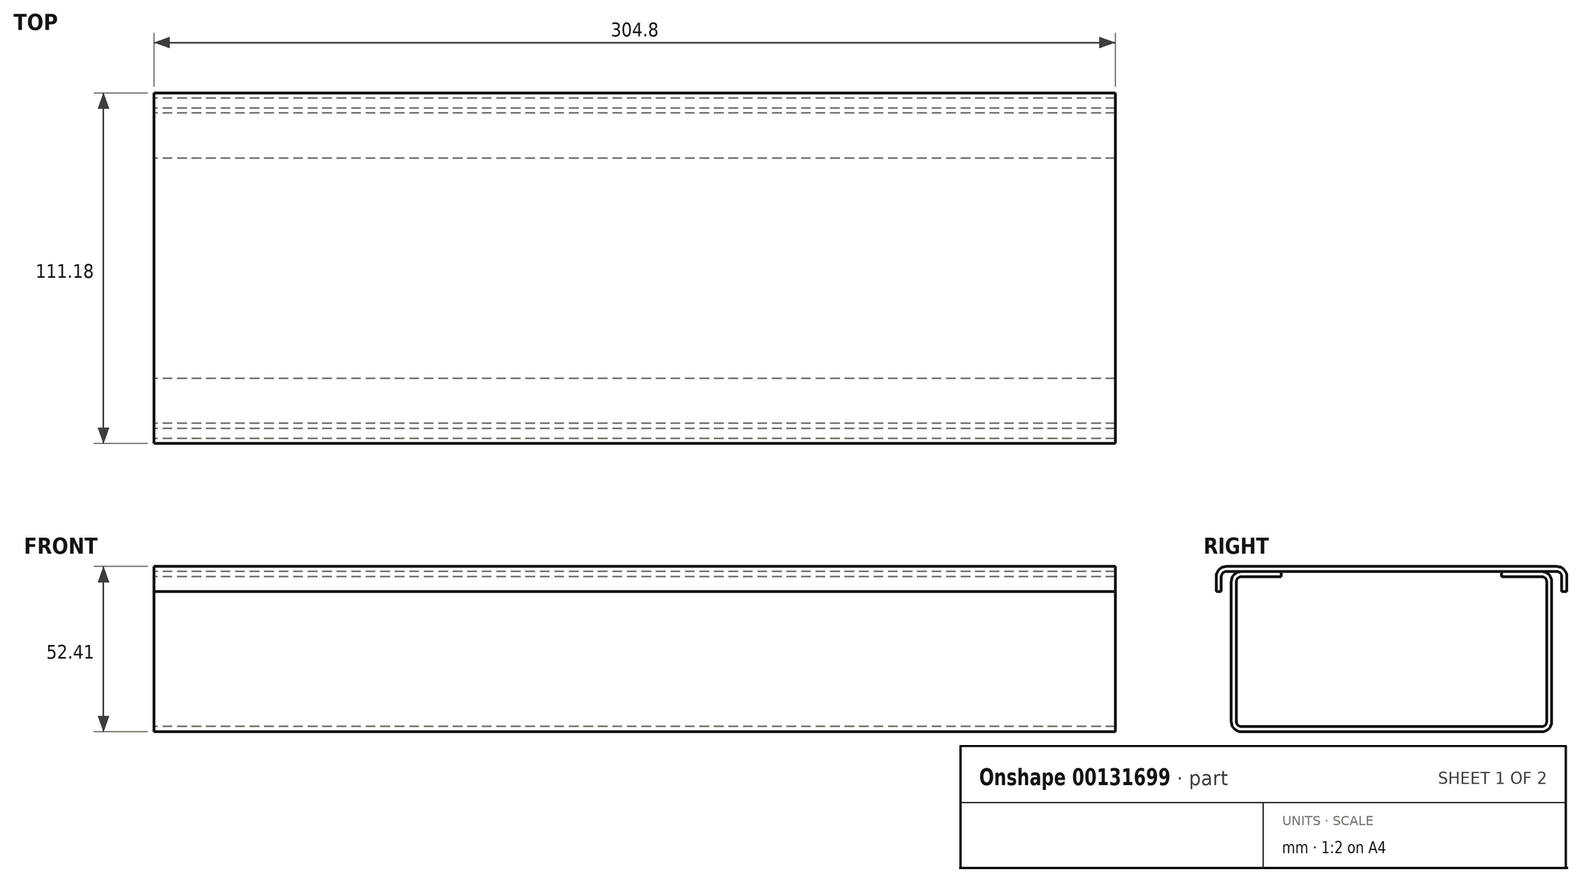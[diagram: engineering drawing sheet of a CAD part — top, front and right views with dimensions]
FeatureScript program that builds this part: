
annotation { "Feature Type Name" : "Feature", "Feature Type Description" : "" }
export const myFeature = defineFeature(function(context is Context, id is Id, definition is map)
    precondition{}
    {
        {
            var Q0;
            Q0=qCreatedBy(makeId("Right.planeOp"),FACE);
            var sketch = newSketch(context, id + "F0", { "sketchPlane" : qUnion([Q0])});
            skLineSegment(sketch, "E0", {"start": v(0, 0) * mm, "end": v(47.6, 0) * mm});
            skLineSegment(sketch, "E1", {"start": v(50.8, 3.2) * mm, "end": v(50.8, 47.6) * mm});
            skPoint(sketch, "E2.visualSharp", {"position": v(50.8, 0) * mm});
            skLineSegment(sketch, "E3", {"start": v(0, 0) * mm, "end": v(0, 60.98) * mm, "construction": true});
            skLineSegment(sketch, "E4", {"start": v(47.6, 50.8) * mm, "end": v(34.93, 50.8) * mm});
            skLineSegment(sketch, "E5.0", {"start": v(47.6, 49.19) * mm, "end": v(34.93, 49.19) * mm});
            skLineSegment(sketch, "E5.1", {"start": v(49.19, 3.2) * mm, "end": v(49.19, 47.6) * mm});
            skLineSegment(sketch, "E5.2", {"start": v(0, 1.61) * mm, "end": v(47.6, 1.61) * mm});
            skLineSegment(sketch, "E6", {"start": v(34.93, 50.8) * mm, "end": v(34.93, 49.19) * mm});
            skPoint(sketch, "E7.visualSharp", {"position": v(49.19, 49.19) * mm});
            skArc(sketch, "E7.filletArc", {"start": v(49.19, 47.6) * mm, "mid": v(48.72, 48.72) * mm, "end": v(47.6, 49.19) * mm});
            skPoint(sketch, "E8.visualSharp", {"position": v(50.8, 50.8) * mm});
            skArc(sketch, "E8.filletArc", {"start": v(50.8, 47.6) * mm, "mid": v(49.86, 49.86) * mm, "end": v(47.6, 50.8) * mm});
            skPoint(sketch, "E9.visualSharp", {"position": v(49.19, 1.61) * mm});
            skArc(sketch, "E9.filletArc", {"start": v(47.6, 1.61) * mm, "mid": v(48.72, 2.08) * mm, "end": v(49.19, 3.2) * mm});
            skArc(sketch, "E10.filletArc", {"start": v(47.6, 0) * mm, "mid": v(49.86, 0.94) * mm, "end": v(50.8, 3.2) * mm});
            skArc(sketch, "E11.MirrorCS", {"start": v(-49.19, 47.6) * mm, "mid": v(-48.72, 48.72) * mm, "end": v(-47.6, 49.19) * mm});
            skArc(sketch, "E12.MirrorCS", {"start": v(-47.6, 0) * mm, "mid": v(-49.86, 0.94) * mm, "end": v(-50.8, 3.2) * mm});
            skArc(sketch, "E13.MirrorCS", {"start": v(-47.6, 1.61) * mm, "mid": v(-48.72, 2.08) * mm, "end": v(-49.19, 3.2) * mm});
            skArc(sketch, "E14.MirrorCS", {"start": v(-50.8, 47.6) * mm, "mid": v(-49.86, 49.86) * mm, "end": v(-47.6, 50.8) * mm});
            skLineSegment(sketch, "E15.MirrorCS", {"start": v(-34.92, 50.8) * mm, "end": v(-34.92, 49.19) * mm});
            skPoint(sketch, "E16.MirrorP", {"position": v(-49.19, 49.19) * mm});
            skPoint(sketch, "E17.MirrorP", {"position": v(-50.8, 0) * mm});
            skLineSegment(sketch, "E18.MirrorCS", {"start": v(-47.6, 50.8) * mm, "end": v(-34.92, 50.8) * mm});
            skLineSegment(sketch, "E19.MirrorCS", {"start": v(0, 1.61) * mm, "end": v(-47.6, 1.61) * mm});
            skPoint(sketch, "E20.MirrorP", {"position": v(-50.8, 50.8) * mm});
            skPoint(sketch, "E21.MirrorP", {"position": v(-49.19, 1.61) * mm});
            skLineSegment(sketch, "E22.MirrorCS", {"start": v(-50.8, 3.2) * mm, "end": v(-50.8, 47.6) * mm});
            skLineSegment(sketch, "E23.MirrorCS", {"start": v(-49.19, 3.2) * mm, "end": v(-49.19, 47.6) * mm});
            skLineSegment(sketch, "E24.MirrorCS", {"start": v(0, 0) * mm, "end": v(-47.6, 0) * mm});
            skLineSegment(sketch, "E25.MirrorCS", {"start": v(-47.6, 49.19) * mm, "end": v(-34.92, 49.19) * mm});
            skSolve(sketch);
        }
        {
            var Q0;
            Q0 = qSketchRegion(id + "F0", true);
            extrude(context, id + "F1", {"entities" : qUnion([Q0]), "depth" : 304.8 * mm});
        }
        {
            var Q0;
            Q0=qCreatedBy(makeId("Right.planeOp"),FACE);
            var sketch = newSketch(context, id + "F2", { "sketchPlane" : qUnion([Q0])});
            skLineSegment(sketch, "E26", {"start": v(0, 0) * mm, "end": v(0, 72.15) * mm, "construction": true});
            skLineSegment(sketch, "E27.0", {"start": v(47.6, 50.8) * mm, "end": v(34.93, 50.8) * mm, "construction": true});
            skLineSegment(sketch, "E28", {"start": v(0, 50.8) * mm, "end": v(52.39, 50.8) * mm});
            skLineSegment(sketch, "E29", {"start": v(53.98, 49.21) * mm, "end": v(53.98, 44.45) * mm});
            skPoint(sketch, "E30.visualSharp", {"position": v(53.98, 50.8) * mm});
            skArc(sketch, "E30.filletArc", {"start": v(53.98, 49.21) * mm, "mid": v(53.51, 50.34) * mm, "end": v(52.39, 50.8) * mm});
            skLineSegment(sketch, "E31.0", {"start": v(55.59, 49.21) * mm, "end": v(55.59, 44.45) * mm});
            skArc(sketch, "E31.1", {"start": v(55.59, 49.21) * mm, "mid": v(54.65, 51.48) * mm, "end": v(52.39, 52.41) * mm});
            skLineSegment(sketch, "E31.2", {"start": v(0, 52.41) * mm, "end": v(52.39, 52.41) * mm});
            skLineSegment(sketch, "E32", {"start": v(53.98, 44.45) * mm, "end": v(55.59, 44.45) * mm});
            skLineSegment(sketch, "E33.MirrorCS", {"start": v(-53.98, 44.45) * mm, "end": v(-55.59, 44.45) * mm});
            skArc(sketch, "E34.MirrorCS", {"start": v(-53.98, 49.21) * mm, "mid": v(-53.51, 50.34) * mm, "end": v(-52.39, 50.8) * mm});
            skLineSegment(sketch, "E35.MirrorCS", {"start": v(0, 50.8) * mm, "end": v(-52.39, 50.8) * mm});
            skPoint(sketch, "E36.MirrorP", {"position": v(-53.98, 50.8) * mm});
            skLineSegment(sketch, "E37.MirrorCS", {"start": v(0, 52.41) * mm, "end": v(-52.39, 52.41) * mm});
            skArc(sketch, "E38.MirrorCS", {"start": v(-55.59, 49.21) * mm, "mid": v(-54.65, 51.48) * mm, "end": v(-52.39, 52.41) * mm});
            skLineSegment(sketch, "E39.MirrorCS", {"start": v(-55.59, 49.21) * mm, "end": v(-55.59, 44.45) * mm});
            skLineSegment(sketch, "E40.MirrorCS", {"start": v(-47.6, 50.8) * mm, "end": v(-34.93, 50.8) * mm, "construction": true});
            skLineSegment(sketch, "E41.MirrorCS", {"start": v(-53.98, 49.21) * mm, "end": v(-53.98, 44.45) * mm});
            skSolve(sketch);
        }
        {
            var Q0;
            Q0 = qSketchRegion(id + "F2", true);
            extrude(context, id + "F3", {"entities" : qUnion([Q0]), "depth" : 304.8 * mm});
        }
    });
